# Revit family: Sanitary_Toilet-Cisterns_Sanindusa_Pack-Sanslim-Frame-With-Dual-Flushing-Cistern-And-To-slim-Plate
name_source: partatom
category: Plumbing Fixtures
revit_build: Autodesk Revit 2018 (Build: 20170223_1515(x64)
units: mm (PartAtom-declared; Revit-internal decimal feet)

## family parameters
Always vertical = Yes
Cut with Voids When Loaded = No
Host = Wall
OmniClass Number = 23.45.00.00
OmniClass Title = Sanitary, Laundry, and Cleaning Equipment
Part Type = Normal
Room Calculation Point = No
Round Connector Dimension = Use Diameter
Shared = No

## types (1)
- SANINDUSA_PackwithdualflushingcisternandplateforwallmountedWC_4193311_485x85_Sanslim
    AssetType = Fixed
    CisternCapacity = 6 Lts
    CisternColor = white
    CisternHeight = Other
    CisternMaterial = PPC
    CodePerformance = EN 14055:2010 CL 1
    Color = Cistern: white. Plate: Chromed
    Constituents = "General content (material included):
 Supporting frame for mounting; wall drain elbow ø 90/90 mm with seal; adapter reduction piece ø 90/110 mm with seal; exterior coated with foam (insulation against condensation of water and decrease in operating noise, fiberglass net, water inlet ½ ""in center upper position, dual flush plate included."
    Cost = 0 $
    Description = Pack with dual flushing cistern and plate for wall mounted WC
    Edition number = 1
    Element Type = CISTERN: A water storage unit attached to a sanitary terminal that is fitted with a device, operated automatically or by the user, that discharges water to cleanse a water closet (toilet) pan, urinal or slop hopper. (BS6100 330 5008)
    Features = Supporting frame for wall-mounted toilets with a concealed flushing cistern. For frontal activation. Used for mounting a dual flush flushing plate already included. The flushing cistern is insulated against condensation. With silent filling valve. Suitable for the installation of toilet bowls with an axial distance of 18 or 23 cm.
    FlushRate = Lowerbound:3 Lts
Upperbound:6 Lts
    FlushType = push
    Installation Instructions = https://www.tec.sanindusa.pt
    InstallationDate = 1900-12-31T23:59:59
    IsAutomaticFlush = FALSE
    IsSingleFlush = FALSE
    Manufacturer = www.sanindusa.pt
    ManufacturerName = Sanindusa
    ManufacturerURL = www.tec.sanindusa.pt
    Material = Cistern: PPC. Plate: ABS
    ModelNumber = 4193311
    ModelReference = Sanslim
    Name = Pack sanslim frame with dual flushing cistern and to-slim plate for wall mounted WC
    NominalHeight = 0 mm  [stored 0 ft]
    NominalLength = 485 mm
    NominalWidth = 85 mm
    Pre-defined type (IFC) = CISTERN
    Product Guid = 66395d02-c5eb-41b6-9436-7e8a658b34b8
    Product data url = https://bimobject.com
    ProductInformation = https://www.tec.sanindusa.pt
    ProductionYear = 2018
    Size = 485x85
    Type (IFC) = IfcSanitaryTerminalType
    URL = www.tec.sanindusa.pt
    Uniclass2015Code = Pr_40_20_93_89
    Uniclass2015Title = WC cisterns
    Uniclass2015Version = Products v1.6
    Version = 1
    WarrantyDescription = https://www.tec.sanindusa.pt
    WarrantyDurationParts = 5
    WarrantyDurationUnit = year
    WarrantyStartDate = 1900-12-31T23:59:59
    Weight = 9.50 kg
    X = 355 mm

note: [stored X ft] marks values corroborated as IEEE doubles in the binary element streams (Revit-internal decimal feet)

## geometry (parser evidence)
native form markers: Sweep x7
no freeform markers — native parametric forms only
